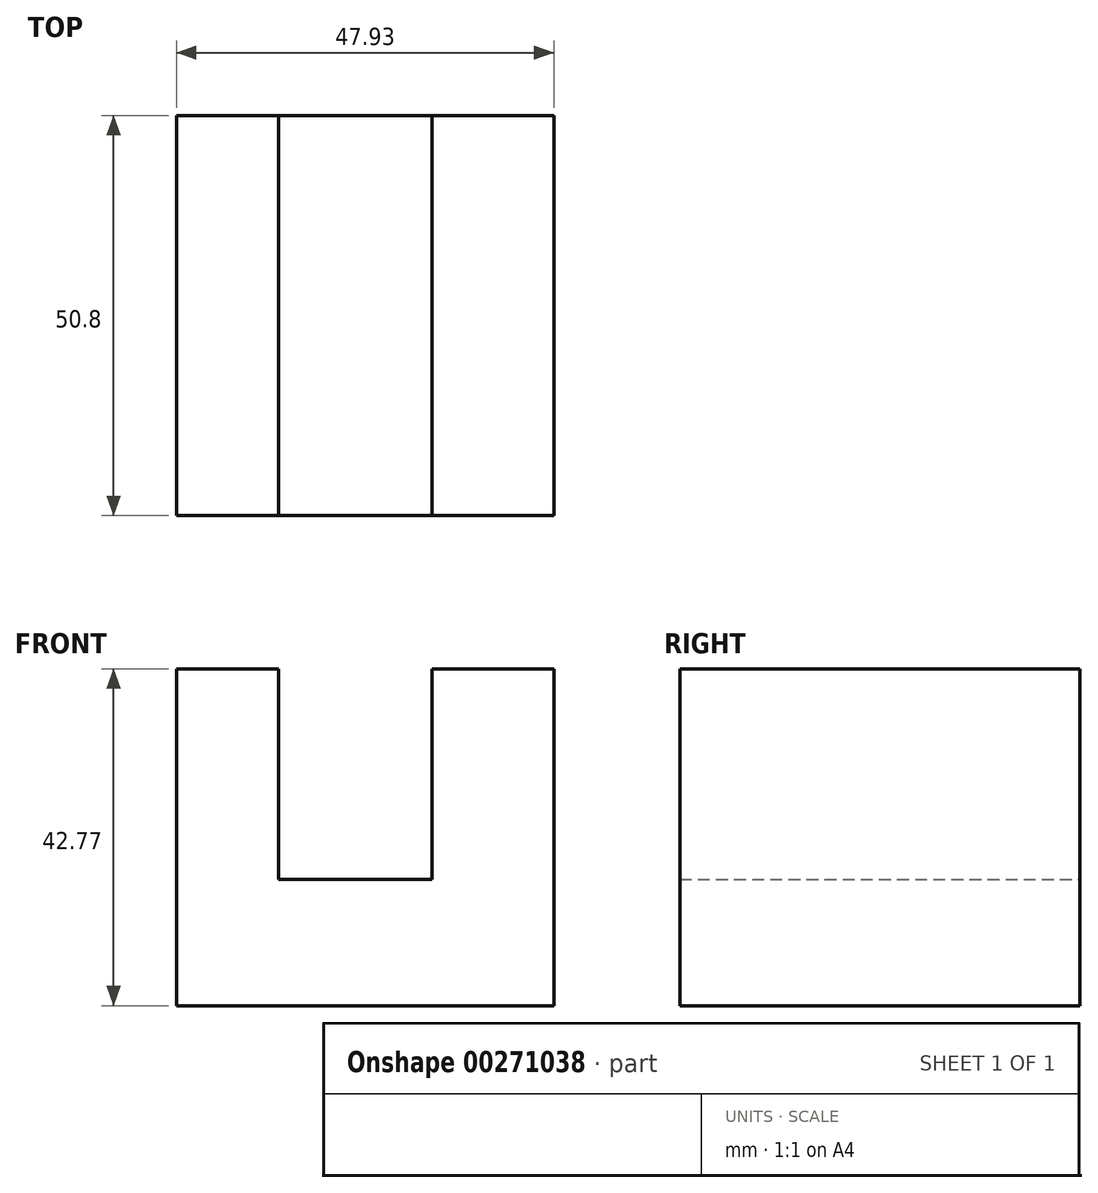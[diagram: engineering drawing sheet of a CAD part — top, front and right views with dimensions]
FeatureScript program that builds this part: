
annotation { "Feature Type Name" : "Feature", "Feature Type Description" : "" }
export const myFeature = defineFeature(function(context is Context, id is Id, definition is map)
    precondition{}
    {
        {
            var Q0;
            Q0=qCreatedBy(makeId("Front.planeOp"),FACE);
            var sketch = newSketch(context, id + "F0", { "sketchPlane" : qUnion([Q0])});
            skLineSegment(sketch, "E0", {"start": v(-69.13, 48.12) * mm, "end": v(-69.13, 5.35) * mm});
            skLineSegment(sketch, "E1", {"start": v(-69.13, 5.35) * mm, "end": v(-21.2, 5.35) * mm});
            skLineSegment(sketch, "E2", {"start": v(-21.2, 5.35) * mm, "end": v(-21.2, 48.12) * mm});
            skLineSegment(sketch, "E3", {"start": v(-21.2, 48.12) * mm, "end": v(-36.66, 48.12) * mm});
            skLineSegment(sketch, "E4", {"start": v(-36.66, 48.12) * mm, "end": v(-36.66, 21.39) * mm});
            skLineSegment(sketch, "E5", {"start": v(-36.66, 21.39) * mm, "end": v(-56.14, 21.39) * mm});
            skLineSegment(sketch, "E6", {"start": v(-56.14, 21.39) * mm, "end": v(-56.14, 48.12) * mm});
            skLineSegment(sketch, "E7", {"start": v(-56.14, 48.12) * mm, "end": v(-69.13, 48.12) * mm});
            skSolve(sketch);
        }
        {
            var Q0;
            Q0 = qSketchRegion(id + "F0", true);
            extrude(context, id + "F1", {"entities" : qUnion([Q0]), "depth" : 50.8 * mm});
        }
    });
